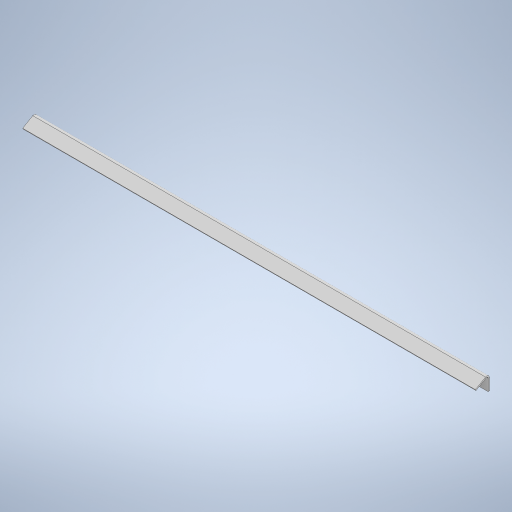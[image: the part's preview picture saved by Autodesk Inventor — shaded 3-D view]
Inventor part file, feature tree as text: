
AUTODESK INVENTOR PART (.ipt)
format: ipt  version: 2023.1 (Build 271208000, 208)  size: 254,976 bytes
history: native  units: mm
features: sheet_metal_op x4, sketch x2, other x2
ambient origin geometry x8: Origin, YZ Plane, XZ Plane, XY Plane, X Axis, Y Axis, Z Axis, Center Point
bodies: Solid1 (feature_tree)
feature tree (8):
  sheet_metal_op  "Face1"
  sheet_metal_op  "Flange1"
  sketch  "Sketch1"  dims[d0=700.0mm]
  other  "Plate1"
  sketch  "Sketch2"  dims[d1=25.0mm d2=2.0mm d3=2.0mm d4=1.0mm d5=4.0mm d6=2.0mm d7=25.0mm d8=120.0deg d9=2.0mm d10=8.0mm d11=2.0mm d12=2.0mm]
  other  "Plate2"
  sheet_metal_op  "Bend1"
  sheet_metal_op  "Corner1"
